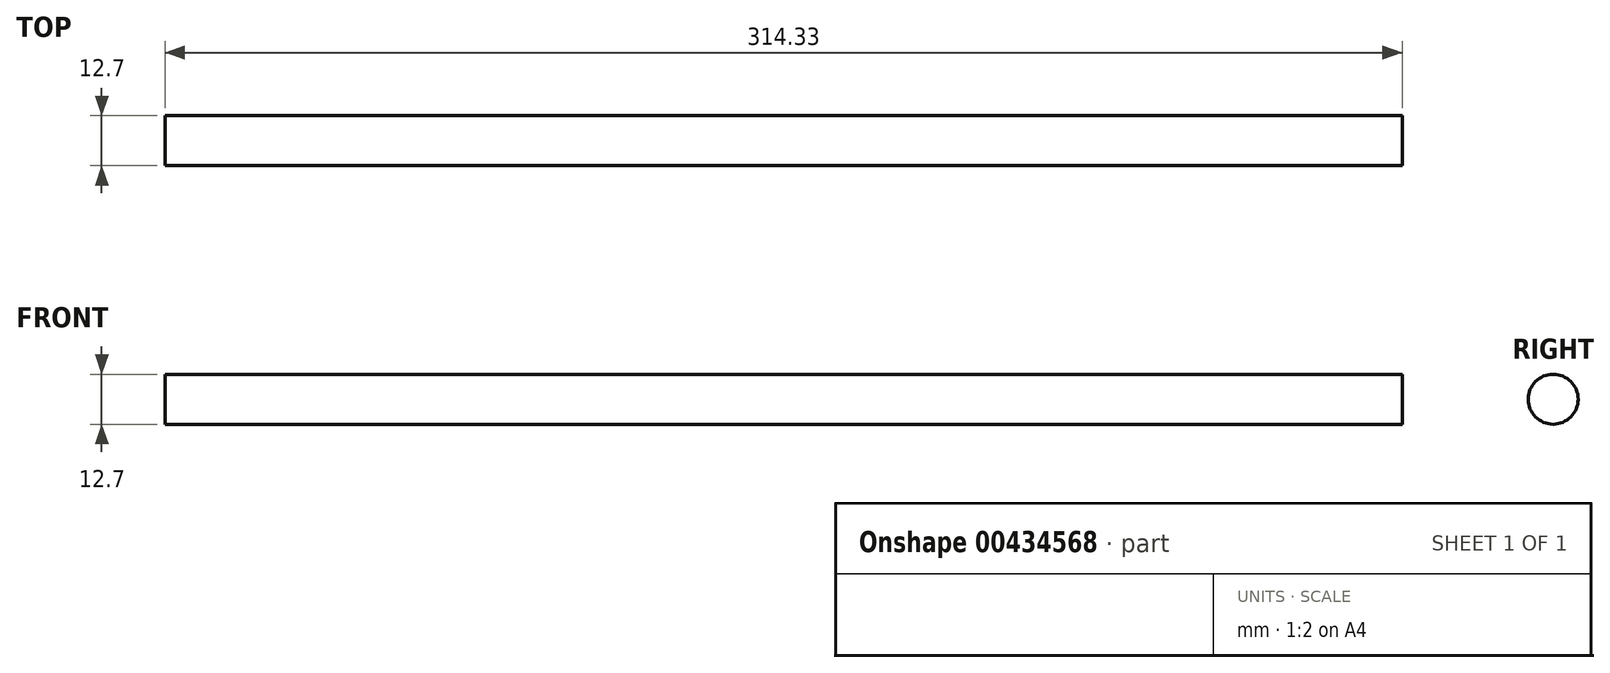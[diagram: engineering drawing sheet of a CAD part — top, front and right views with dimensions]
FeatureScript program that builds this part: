
annotation { "Feature Type Name" : "Feature", "Feature Type Description" : "" }
export const myFeature = defineFeature(function(context is Context, id is Id, definition is map)
    precondition{}
    {
        {
            var Q0;
            Q0=qCreatedBy(makeId("Right.planeOp"),FACE);
            var sketch = newSketch(context, id + "F0", { "sketchPlane" : qUnion([Q0])});
            skCircle(sketch, "E0", {"center": v(-27.45, 19.3) * mm, "radius": 6.35 * mm});
            skSolve(sketch);
        }
        {
            var Q0;
            Q0=makeQuery(id+"F0.imprint","IMPRINT",FACE,{"disambiguationData":[TD([[makeQuery(id+"F0.imprint","IMPRINT",EDGE,{"derivedFrom":sQuery(id+"F0.wireOp",EDGE,"E0")}),1.0]])]});
            extrude(context, id + "F1", {"entities" : qUnion([Q0]), "depth" : 314.32 * mm});
        }
    });
